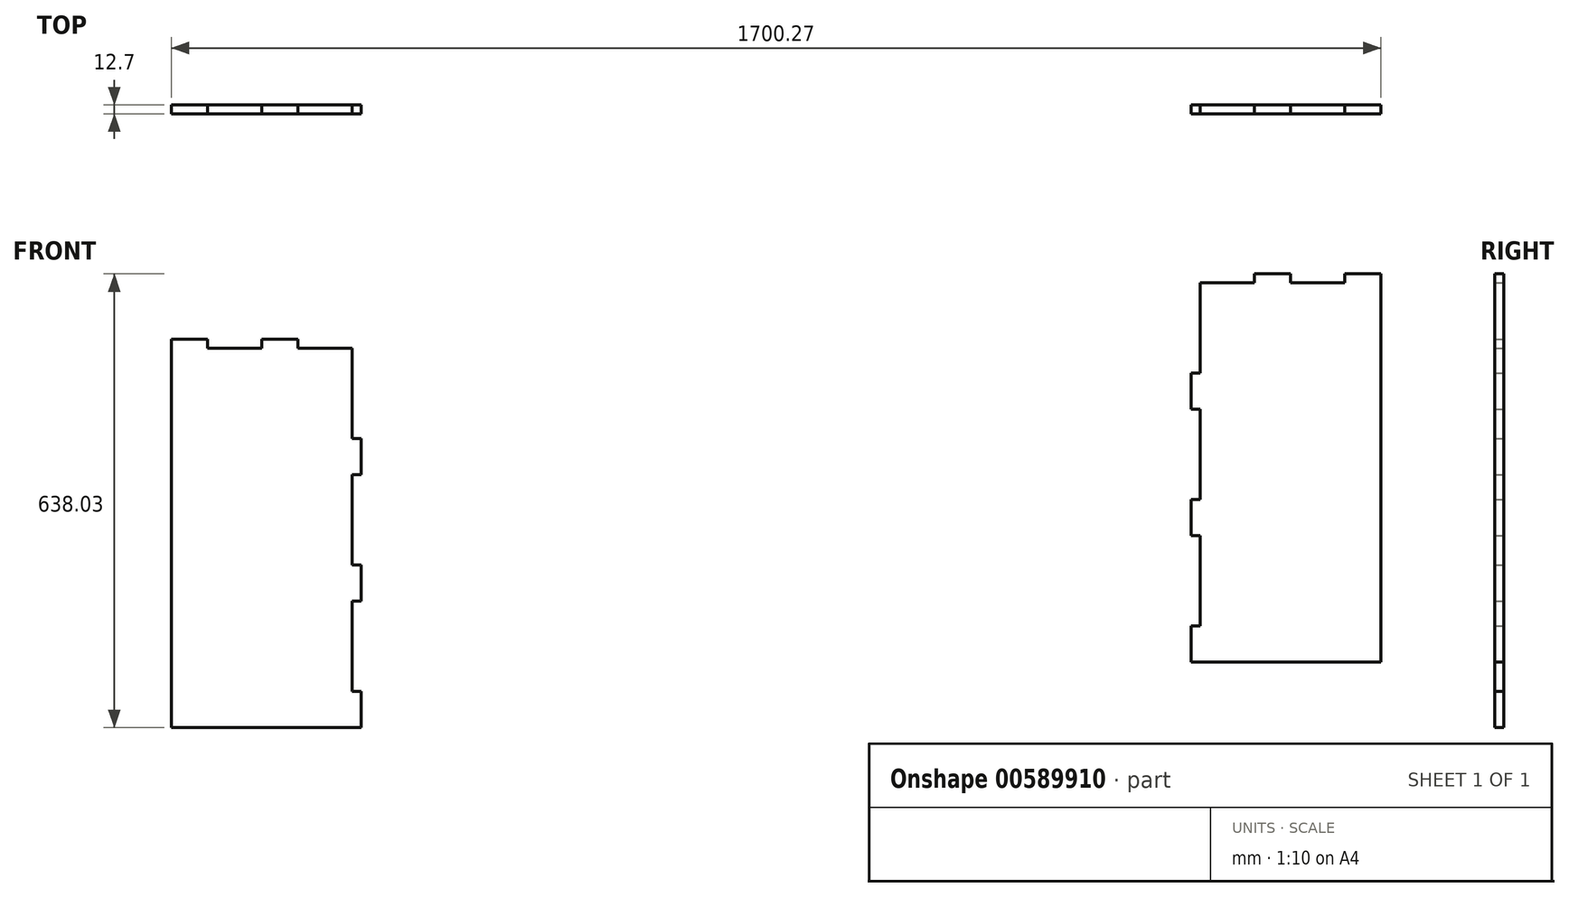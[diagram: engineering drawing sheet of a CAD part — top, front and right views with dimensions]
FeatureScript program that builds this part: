
annotation { "Feature Type Name" : "Feature", "Feature Type Description" : "" }
export const myFeature = defineFeature(function(context is Context, id is Id, definition is map)
    precondition{}
    {
        {
            var Q0;
            Q0=qCreatedBy(makeId("Front.planeOp"),FACE);
            var sketch = newSketch(context, id + "F0", { "sketchPlane" : qUnion([Q0])});
            skLineSegment(sketch, "E0.bottom", {"start": v(-930.7, -266.32) * mm, "end": v(-676.7, -266.32) * mm});
            skLineSegment(sketch, "E0.top", {"start": v(-879.9, 267.08) * mm, "end": v(-803.7, 267.08) * mm});
            skLineSegment(sketch, "E0.left", {"start": v(-930.7, -266.32) * mm, "end": v(-930.7, 267.08) * mm});
            skLineSegment(sketch, "E0.right", {"start": v(-676.7, -215.52) * mm, "end": v(-676.7, -88.52) * mm});
            skLineSegment(sketch, "E1.bottom", {"start": v(515.57, -174.39) * mm, "end": v(769.57, -174.39) * mm});
            skLineSegment(sketch, "E1.top", {"start": v(515.57, 359.01) * mm, "end": v(591.77, 359.01) * mm});
            skLineSegment(sketch, "E1.left", {"start": v(515.57, -123.59) * mm, "end": v(515.57, 3.41) * mm});
            skLineSegment(sketch, "E1.right", {"start": v(769.57, -174.39) * mm, "end": v(769.57, 359.01) * mm});
            skLineSegment(sketch, "E2.bottom", {"start": v(-676.7, 140.08) * mm, "end": v(-664, 140.08) * mm});
            skLineSegment(sketch, "E2.top", {"start": v(-676.7, 89.28) * mm, "end": v(-664, 89.28) * mm});
            skLineSegment(sketch, "E2.right", {"start": v(-664, 140.08) * mm, "end": v(-664, 89.28) * mm});
            skLineSegment(sketch, "E3.bottom", {"start": v(-676.7, -37.72) * mm, "end": v(-664, -37.72) * mm});
            skLineSegment(sketch, "E3.top", {"start": v(-676.7, -88.52) * mm, "end": v(-664, -88.52) * mm});
            skLineSegment(sketch, "E3.right", {"start": v(-664, -37.72) * mm, "end": v(-664, -88.52) * mm});
            skLineSegment(sketch, "E4.bottom", {"start": v(-676.7, -215.52) * mm, "end": v(-664, -215.52) * mm});
            skLineSegment(sketch, "E4.top", {"start": v(-676.7, -266.32) * mm, "end": v(-664, -266.32) * mm});
            skLineSegment(sketch, "E4.right", {"start": v(-664, -215.52) * mm, "end": v(-664, -266.32) * mm});
            skLineSegment(sketch, "E5.bottom", {"start": v(515.57, 232.01) * mm, "end": v(502.87, 232.01) * mm});
            skLineSegment(sketch, "E5.top", {"start": v(515.57, 181.21) * mm, "end": v(502.87, 181.21) * mm});
            skLineSegment(sketch, "E5.right", {"start": v(502.87, 232.01) * mm, "end": v(502.87, 181.21) * mm});
            skLineSegment(sketch, "E6.bottom", {"start": v(515.57, 54.21) * mm, "end": v(502.87, 54.21) * mm});
            skLineSegment(sketch, "E6.top", {"start": v(515.57, 3.41) * mm, "end": v(502.87, 3.41) * mm});
            skLineSegment(sketch, "E6.right", {"start": v(502.87, 54.21) * mm, "end": v(502.87, 3.41) * mm});
            skLineSegment(sketch, "E7.bottom", {"start": v(515.57, -123.59) * mm, "end": v(502.87, -123.59) * mm});
            skLineSegment(sketch, "E7.top", {"start": v(515.57, -174.39) * mm, "end": v(502.87, -174.39) * mm});
            skLineSegment(sketch, "E7.right", {"start": v(502.87, -123.59) * mm, "end": v(502.87, -174.39) * mm});
            skLineSegment(sketch, "E8.trimOffspring", {"start": v(515.57, 232.01) * mm, "end": v(515.57, 359.01) * mm});
            skLineSegment(sketch, "E9.trimOffspring", {"start": v(515.57, 54.21) * mm, "end": v(515.57, 181.21) * mm});
            skLineSegment(sketch, "E10.trimOffspring", {"start": v(-676.7, 140.08) * mm, "end": v(-676.7, 267.08) * mm});
            skLineSegment(sketch, "E11.trimOffspring", {"start": v(-676.7, -37.72) * mm, "end": v(-676.7, 89.28) * mm});
            skLineSegment(sketch, "E12.top", {"start": v(-930.7, 279.78) * mm, "end": v(-879.9, 279.78) * mm});
            skLineSegment(sketch, "E12.left", {"start": v(-930.7, 267.08) * mm, "end": v(-930.7, 279.78) * mm});
            skLineSegment(sketch, "E12.right", {"start": v(-879.9, 267.08) * mm, "end": v(-879.9, 279.78) * mm});
            skLineSegment(sketch, "E13.top", {"start": v(-803.7, 279.78) * mm, "end": v(-752.9, 279.78) * mm});
            skLineSegment(sketch, "E13.left", {"start": v(-803.7, 267.08) * mm, "end": v(-803.7, 279.78) * mm});
            skLineSegment(sketch, "E13.right", {"start": v(-752.9, 267.08) * mm, "end": v(-752.9, 279.78) * mm});
            skLineSegment(sketch, "E14.top", {"start": v(591.77, 371.71) * mm, "end": v(642.57, 371.71) * mm});
            skLineSegment(sketch, "E14.left", {"start": v(591.77, 359.01) * mm, "end": v(591.77, 371.71) * mm});
            skLineSegment(sketch, "E14.right", {"start": v(642.57, 359.01) * mm, "end": v(642.57, 371.71) * mm});
            skLineSegment(sketch, "E15.top", {"start": v(769.57, 371.71) * mm, "end": v(718.77, 371.71) * mm});
            skLineSegment(sketch, "E15.left", {"start": v(769.57, 359.01) * mm, "end": v(769.57, 371.71) * mm});
            skLineSegment(sketch, "E15.right", {"start": v(718.77, 359.01) * mm, "end": v(718.77, 371.71) * mm});
            skLineSegment(sketch, "E16.trimOffspring", {"start": v(-752.9, 267.08) * mm, "end": v(-676.7, 267.08) * mm});
            skLineSegment(sketch, "E17.trimOffspring", {"start": v(642.57, 359.01) * mm, "end": v(718.77, 359.01) * mm});
            skSolve(sketch);
        }
        {
            var Q0;
            Q0 = qSketchRegion(id + "F0", true);
            extrude(context, id + "F1", {"entities" : qUnion([Q0]), "depth" : 12.7 * mm, "offsetDistance" : 25.4 * mm});
        }
    });
